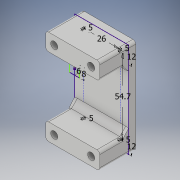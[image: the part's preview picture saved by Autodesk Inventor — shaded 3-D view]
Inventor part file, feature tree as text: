
AUTODESK INVENTOR PART (.ipt)
format: ipt  version: 2018 (Build 220112000, 112)  size: 169,472 bytes
history: native  units: in
note: dims shown in document units (in); Inventor stores cm internally (conversion verified against a paired STEP export)
features: extrude x6, sketch x1, fillet x1, chamfer x1
ambient origin geometry x8: Origin, YZ Plane, XZ Plane, XY Plane, X Axis, Y Axis, Z Axis, Center Point
bodies: Solid1 (feature_tree)
feature tree (9):
  sketch  "Sketch1"  dims[d0=1.0236in d1=2.1535in d2=0.1969in d3=0.1969in d4=0.1969in d5=0.1969in d6=0.2362in d7=0.4724in d8=0.4724in d9=0.1969in d10=0.0in d11=0.7992in d12=0.0in d13=0.7992in d14=0.0in d15=0.1969in d16=0.0in d17=0.1969in d18=0.0in d19=0.0787in d20=0.1654in d21=0.0787in d22=45.0deg d23=0.315in d24=0.1969in d25=0.0in]
  extrude  "Extrusion1"  Depth=0.1969in
  extrude  "Extrusion2"  Depth=0.1969in
  extrude  "Extrusion3"  Depth=0.1969in
  extrude  "Extrusion4"  Depth=0.1969in
  extrude  "Extrusion5"  Depth=0.1969in
  fillet  "Fillet1"  Radius=0.2362in
  chamfer  "Chamfer1"  Distance=0.4724in
  extrude  "Extrusion6"  Depth=0.1969in
